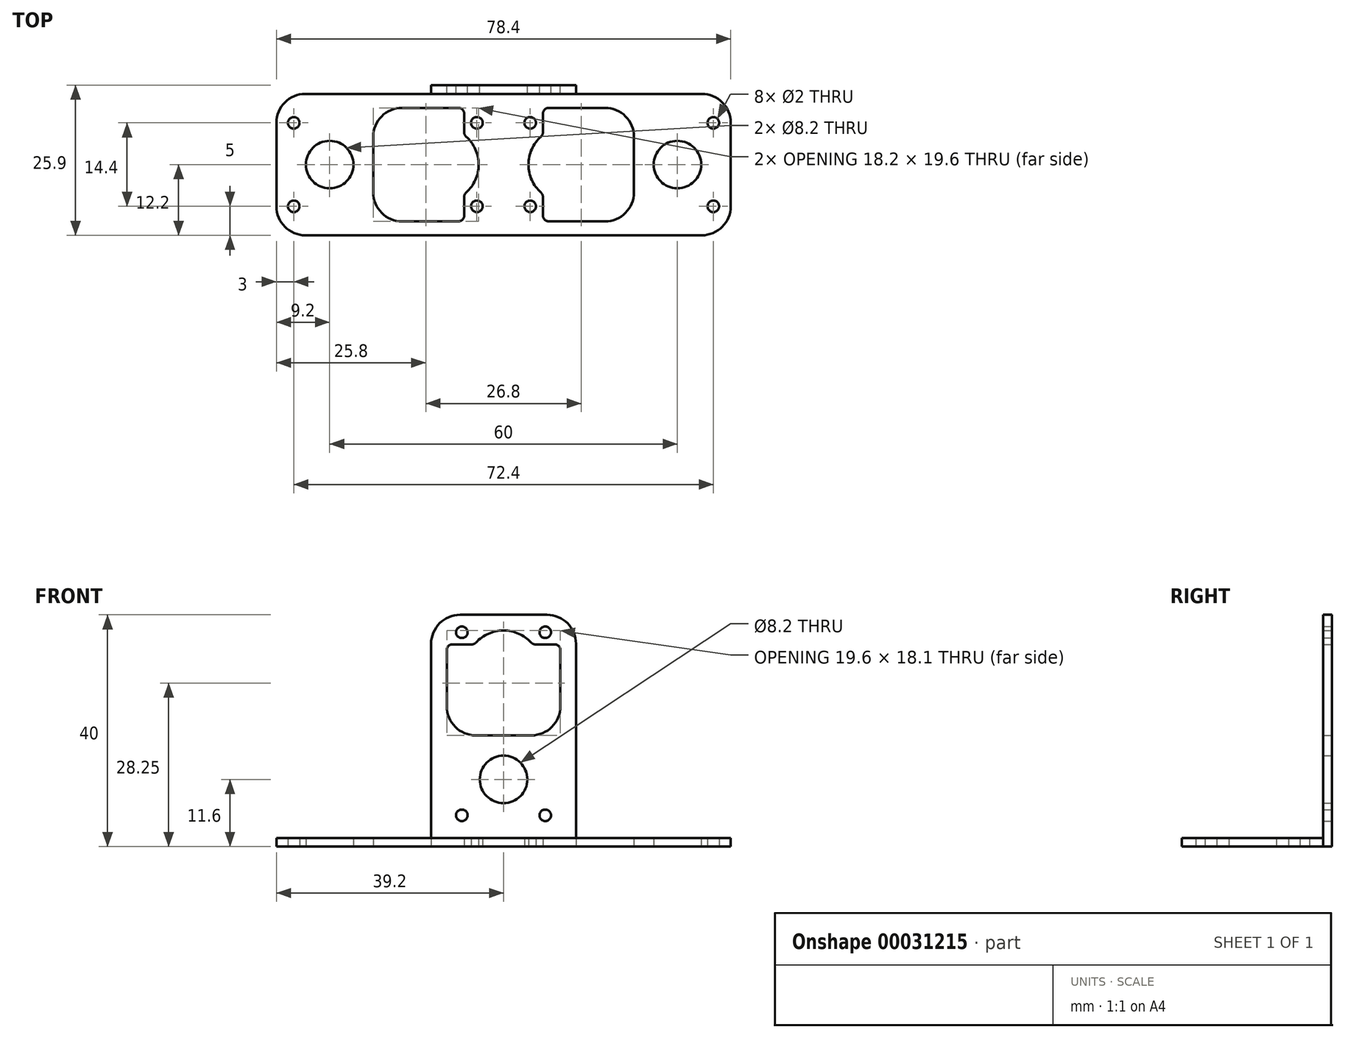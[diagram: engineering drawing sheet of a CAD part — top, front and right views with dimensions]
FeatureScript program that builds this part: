
annotation { "Feature Type Name" : "Feature", "Feature Type Description" : "" }
export const myFeature = defineFeature(function(context is Context, id is Id, definition is map)
    precondition{}
    {
        {
            var Q0;
            Q0=qCreatedBy(makeId("Top.planeOp"),FACE);
            var sketch = newSketch(context, id + "F0", { "sketchPlane" : qUnion([Q0])});
            skLineSegment(sketch, "E0.bottom", {"start": v(39.2, -12.2) * mm, "end": v(-39.2, -12.2) * mm});
            skLineSegment(sketch, "E0.top", {"start": v(39.2, 12.2) * mm, "end": v(-39.2, 12.2) * mm});
            skLineSegment(sketch, "E0.left", {"start": v(39.2, -12.2) * mm, "end": v(39.2, 12.2) * mm});
            skLineSegment(sketch, "E0.right", {"start": v(-39.2, -12.2) * mm, "end": v(-39.2, 12.2) * mm});
            skPoint(sketch, "E0.middle", {"position": v(0, 0) * mm});
            skCircle(sketch, "E1", {"center": v(-30, 0) * mm, "radius": 4.1 * mm});
            skCircle(sketch, "E2", {"center": v(-36.2, 7.2) * mm, "radius": 1 * mm});
            skCircle(sketch, "E3", {"center": v(-4.6, 7.2) * mm, "radius": 1 * mm});
            skLineSegment(sketch, "E4.bottom", {"start": v(-17.5, 9.8) * mm, "end": v(-7.8, 9.8) * mm});
            skLineSegment(sketch, "E4.top", {"start": v(-17.5, -9.8) * mm, "end": v(-7.8, -9.8) * mm});
            skLineSegment(sketch, "E4.left", {"start": v(-22.5, 4.8) * mm, "end": v(-22.5, -4.8) * mm});
            skLineSegment(sketch, "E4.right", {"start": v(-6.8, 8.8) * mm, "end": v(-6.8, 5.6) * mm});
            skPoint(sketch, "E4.middle", {"position": v(-14.65, 0) * mm});
            skPoint(sketch, "E5.visualSharp", {"position": v(-22.5, 9.8) * mm});
            skArc(sketch, "E5.filletArc", {"start": v(-17.5, 9.8) * mm, "mid": v(-21.04, 8.34) * mm, "end": v(-22.5, 4.8) * mm});
            skPoint(sketch, "E6.visualSharp", {"position": v(-22.5, -9.8) * mm});
            skArc(sketch, "E6.filletArc", {"start": v(-22.5, -4.8) * mm, "mid": v(-21.04, -8.34) * mm, "end": v(-17.5, -9.8) * mm});
            skPoint(sketch, "E7.visualSharp", {"position": v(-6.8, 9.8) * mm});
            skArc(sketch, "E7.filletArc", {"start": v(-6.8, 8.8) * mm, "mid": v(-7.1, 9.5) * mm, "end": v(-7.8, 9.8) * mm});
            skPoint(sketch, "E8.visualSharp", {"position": v(-6.8, -9.8) * mm});
            skArc(sketch, "E8.filletArc", {"start": v(-7.8, -9.8) * mm, "mid": v(-7.1, -9.5) * mm, "end": v(-6.8, -8.8) * mm});
            skCircle(sketch, "E9.MirrorC", {"center": v(-36.2, -7.2) * mm, "radius": 1 * mm});
            skCircle(sketch, "E10.MirrorC", {"center": v(-4.6, -7.2) * mm, "radius": 1 * mm});
            skArc(sketch, "E11.MirrorCS", {"start": v(6.8, 8.8) * mm, "mid": v(7.1, 9.5) * mm, "end": v(7.8, 9.8) * mm});
            skArc(sketch, "E12.MirrorCS", {"start": v(7.8, -9.8) * mm, "mid": v(7.1, -9.5) * mm, "end": v(6.8, -8.8) * mm});
            skCircle(sketch, "E13.MirrorC", {"center": v(4.6, -7.2) * mm, "radius": 1 * mm});
            skArc(sketch, "E14.MirrorCS", {"start": v(22.5, -4.8) * mm, "mid": v(21.04, -8.34) * mm, "end": v(17.5, -9.8) * mm});
            skArc(sketch, "E15.MirrorCS", {"start": v(17.5, 9.8) * mm, "mid": v(21.04, 8.34) * mm, "end": v(22.5, 4.8) * mm});
            skLineSegment(sketch, "E16.MirrorCS", {"start": v(6.8, 8.8) * mm, "end": v(6.8, 5.6) * mm});
            skPoint(sketch, "E17.MirrorP", {"position": v(6.8, -9.8) * mm});
            skLineSegment(sketch, "E18.MirrorCS", {"start": v(17.5, 9.8) * mm, "end": v(7.8, 9.8) * mm});
            skCircle(sketch, "E19.MirrorC", {"center": v(4.6, 7.2) * mm, "radius": 1 * mm});
            skPoint(sketch, "E20.MirrorP", {"position": v(6.8, 9.8) * mm});
            skPoint(sketch, "E21.MirrorP", {"position": v(14.65, 0) * mm});
            skCircle(sketch, "E22.MirrorC", {"center": v(36.2, -7.2) * mm, "radius": 1 * mm});
            skCircle(sketch, "E23.MirrorC", {"center": v(36.2, 7.2) * mm, "radius": 1 * mm});
            skCircle(sketch, "E24.MirrorC", {"center": v(30, 0) * mm, "radius": 4.1 * mm});
            skLineSegment(sketch, "E25.MirrorCS", {"start": v(22.5, 4.8) * mm, "end": v(22.5, -4.8) * mm});
            skPoint(sketch, "E26.MirrorP", {"position": v(22.5, -9.8) * mm});
            skLineSegment(sketch, "E27.MirrorCS", {"start": v(17.5, -9.8) * mm, "end": v(7.8, -9.8) * mm});
            skPoint(sketch, "E28.MirrorP", {"position": v(22.5, 9.8) * mm});
            skArc(sketch, "E29", {"start": v(-6.47, -4.84) * mm, "mid": v(-4.3, 0) * mm, "end": v(-6.47, 4.84) * mm});
            skLineSegment(sketch, "E30.trimOffspring", {"start": v(-6.8, -5.6) * mm, "end": v(-6.8, -8.8) * mm});
            skPoint(sketch, "E31.visualSharp", {"position": v(-6.8, 5.12) * mm});
            skArc(sketch, "E31.filletArc", {"start": v(-6.8, 5.6) * mm, "mid": v(-6.71, 5.18) * mm, "end": v(-6.47, 4.84) * mm});
            skPoint(sketch, "E32.visualSharp", {"position": v(-6.8, -5.12) * mm});
            skArc(sketch, "E32.filletArc", {"start": v(-6.47, -4.84) * mm, "mid": v(-6.71, -5.18) * mm, "end": v(-6.8, -5.6) * mm});
            skArc(sketch, "E33.MirrorCS", {"start": v(6.8, 5.6) * mm, "mid": v(6.71, 5.18) * mm, "end": v(6.47, 4.84) * mm});
            skArc(sketch, "E34.MirrorCS", {"start": v(6.47, -4.84) * mm, "mid": v(4.3, 0) * mm, "end": v(6.47, 4.84) * mm});
            skPoint(sketch, "E35.MirrorP", {"position": v(6.8, 5.12) * mm});
            skPoint(sketch, "E36.MirrorP", {"position": v(6.8, -5.12) * mm});
            skArc(sketch, "E37.MirrorCS", {"start": v(6.47, -4.84) * mm, "mid": v(6.71, -5.18) * mm, "end": v(6.8, -5.6) * mm});
            skLineSegment(sketch, "E38.trimOffspring", {"start": v(6.8, -5.6) * mm, "end": v(6.8, -8.8) * mm});
            skSolve(sketch);
        }
        {
            var Q0;
            Q0 = qSketchRegion(id + "F0", true);
            extrude(context, id + "F1", {"entities" : qUnion([Q0]), "depth" : 1.5 * mm});
        }
        {
            var Q0;
            Q0=qCreatedBy(makeId("Top.planeOp"),FACE);
            var sketch = newSketch(context, id + "F2", { "sketchPlane" : qUnion([Q0])});
            skLineSegment(sketch, "E39.bottom", {"start": v(12.5, 12.2) * mm, "end": v(-12.5, 12.2) * mm});
            skLineSegment(sketch, "E39.top", {"start": v(12.5, 13.7) * mm, "end": v(-12.5, 13.7) * mm});
            skLineSegment(sketch, "E39.left", {"start": v(12.5, 12.2) * mm, "end": v(12.5, 13.7) * mm});
            skLineSegment(sketch, "E39.right", {"start": v(-12.5, 12.2) * mm, "end": v(-12.5, 13.7) * mm});
            skPoint(sketch, "E39.middle", {"position": v(0, 12.95) * mm});
            skLineSegment(sketch, "E40.0", {"start": v(39.2, 12.2) * mm, "end": v(-39.2, 12.2) * mm, "construction": true});
            skSolve(sketch);
        }
        {
            var Q0;
            Q0 = qSketchRegion(id + "F2", true);
            extrude(context, id + "F3", {"entities" : qUnion([Q0]), "operationType" : NewBodyOperationType.ADD, "depth" : 40 * mm});
        }
        {
            var Q0;
            Q0=makeQuery(id+"F3.opExtrude","SWEPT_FACE",FACE,{"disambiguationData":[OSD([sQuery(id+"F2.wireOp",EDGE,"E39.top")])]});
            var sketch = newSketch(context, id + "F4", { "sketchPlane" : qUnion([Q0])});
            skLineSegment(sketch, "E41", {"start": v(-12.5, 20) * mm, "end": v(12.5, 20) * mm, "construction": true});
            skCircle(sketch, "E42", {"center": v(7.2, 37) * mm, "radius": 1 * mm});
            skCircle(sketch, "E43", {"center": v(7.2, 5.4) * mm, "radius": 1 * mm});
            skCircle(sketch, "E44", {"center": v(0, 11.6) * mm, "radius": 4.1 * mm});
            skLineSegment(sketch, "E45.bottom", {"start": v(8.8, 34.9) * mm, "end": v(5.5, 34.9) * mm});
            skLineSegment(sketch, "E45.top", {"start": v(4.8, 19.2) * mm, "end": v(-4.8, 19.2) * mm});
            skLineSegment(sketch, "E45.left", {"start": v(9.8, 33.9) * mm, "end": v(9.8, 24.2) * mm});
            skLineSegment(sketch, "E45.right", {"start": v(-9.8, 33.9) * mm, "end": v(-9.8, 24.2) * mm});
            skPoint(sketch, "E45.middle", {"position": v(0, 27.05) * mm});
            skPoint(sketch, "E46.visualSharp", {"position": v(-9.8, 19.2) * mm});
            skArc(sketch, "E46.filletArc", {"start": v(-9.8, 24.2) * mm, "mid": v(-8.34, 20.66) * mm, "end": v(-4.8, 19.2) * mm});
            skPoint(sketch, "E47.visualSharp", {"position": v(9.8, 19.2) * mm});
            skArc(sketch, "E47.filletArc", {"start": v(4.8, 19.2) * mm, "mid": v(8.34, 20.66) * mm, "end": v(9.8, 24.2) * mm});
            skPoint(sketch, "E48.visualSharp", {"position": v(9.8, 34.9) * mm});
            skArc(sketch, "E48.filletArc", {"start": v(9.8, 33.9) * mm, "mid": v(9.5, 34.6) * mm, "end": v(8.8, 34.9) * mm});
            skPoint(sketch, "E49.visualSharp", {"position": v(-9.8, 34.9) * mm});
            skArc(sketch, "E49.filletArc", {"start": v(-8.8, 34.9) * mm, "mid": v(-9.5, 34.6) * mm, "end": v(-9.8, 33.9) * mm});
            skCircle(sketch, "E50.MirrorC", {"center": v(-7.2, 37) * mm, "radius": 1 * mm});
            skCircle(sketch, "E51.MirrorC", {"center": v(-7.2, 5.4) * mm, "radius": 1 * mm});
            skArc(sketch, "E52", {"start": v(4.77, 35.22) * mm, "mid": v(0, 37.3) * mm, "end": v(-4.77, 35.22) * mm});
            skLineSegment(sketch, "E53.trimOffspring", {"start": v(-5.5, 34.9) * mm, "end": v(-8.8, 34.9) * mm});
            skPoint(sketch, "E54.visualSharp", {"position": v(-5.04, 34.9) * mm});
            skArc(sketch, "E54.filletArc", {"start": v(-5.5, 34.9) * mm, "mid": v(-5.1, 34.98) * mm, "end": v(-4.77, 35.22) * mm});
            skPoint(sketch, "E55.visualSharp", {"position": v(5.04, 34.9) * mm});
            skArc(sketch, "E55.filletArc", {"start": v(4.77, 35.22) * mm, "mid": v(5.1, 34.98) * mm, "end": v(5.5, 34.9) * mm});
            skSolve(sketch);
        }
        {
            var Q0;
            Q0 = qSketchRegion(id + "F4", true);
            extrude(context, id + "F5", {"entities" : qUnion([Q0]), "operationType" : NewBodyOperationType.REMOVE, "endBound" : BoundingType.UP_TO_NEXT, "oppositeDirection" : true, "depth" : 25 * mm});
        }
        {
            var Q0;
            Q0=makeQuery(id+"F1.opExtrude","SWEPT_EDGE",EDGE,{"disambiguationData":[OSD([sQuery(id+"F0.wireOp",EDGE,"E0.top"),sQuery(id+"F0.wireOp",EDGE,"E0.right")])]});
            var Q1;
            Q1=makeQuery(id+"F1.opExtrude","SWEPT_EDGE",EDGE,{"disambiguationData":[OSD([sQuery(id+"F0.wireOp",EDGE,"E0.bottom"),sQuery(id+"F0.wireOp",EDGE,"E0.right")])]});
            var Q2;
            Q2=makeQuery(id+"F1.opExtrude","SWEPT_EDGE",EDGE,{"disambiguationData":[OSD([sQuery(id+"F0.wireOp",EDGE,"E0.top"),sQuery(id+"F0.wireOp",EDGE,"E0.left")])]});
            var Q3;
            Q3=makeQuery(id+"F1.opExtrude","SWEPT_EDGE",EDGE,{"disambiguationData":[OSD([sQuery(id+"F0.wireOp",EDGE,"E0.bottom"),sQuery(id+"F0.wireOp",EDGE,"E0.left")])]});
            var Q4;
            Q4=makeQuery(id+"F3.opExtrude","CAP_EDGE",EDGE,{"disambiguationData":[OSD([sQuery(id+"F2.wireOp",EDGE,"E39.right")])],"isStart":false});
            var Q5;
            Q5=makeQuery(id+"F3.opExtrude","CAP_EDGE",EDGE,{"disambiguationData":[OSD([sQuery(id+"F2.wireOp",EDGE,"E39.left")])],"isStart":false});
            fillet(context, id + "F6", {"entities" : qUnion([Q0, Q1, Q2, Q3, Q4, Q5]), "radius" : 5 * mm, "tangentPropagation" : true, "allowEdgeOverflow" : false});
        }
    });
